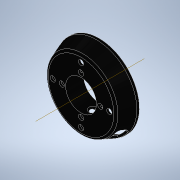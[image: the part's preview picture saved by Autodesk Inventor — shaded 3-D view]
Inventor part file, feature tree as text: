
AUTODESK INVENTOR PART (.ipt)
format: ipt  version: 2022 (Build 260153000, 153)  size: 232,448 bytes
history: native  units: in
note: dims shown in document units (in); Inventor stores cm internally (conversion verified against a paired STEP export)
features: sketch x3, extrude x2, revolve x1, fillet x1, shell x1, plane x1
ambient origin geometry x8: Origin, YZ Plane, XZ Plane, XY Plane, X Axis, Y Axis, Z Axis, Center Point
bodies: Solid1 (feature_tree)
feature tree (9):
  revolve  "Revolution1"  [1 undecoded]
  fillet  "Fillet1"  Radius=0.0787in
  shell  "Shell1"  Thickness=1.063in
  extrude  "Extrusion1"  TaperAngle=90.0deg  [1 undecoded]
  plane  "Work Plane1"
  extrude  "Extrusion2"  Depth=0.1575in
  sketch  "Sketch1"  dims[d0=1.2402in d1=0.5512in d2=0.0787in d3=1.063in]
  sketch  "Sketch2"  dims[d4=0.4724in d5=90.0deg]
  sketch  "Sketch3"  dims[d6=0.0787in d7=1.1811in d8=1.7323in d9=0.1575in d10=0.1575in d11=1.5748in d13=360.0deg d15=0.0625in d16=1.0in d17=0.0in d18=0.1969in d19=90.0deg d20=0.315in d21=2.0in d22=0.0in]
note: 2 required parameter values undecoded (feature->parameter linkage not recoverable at this tier; creation-order binding heuristic only, values carry confidence <= 0.55)